# Revit family: Condensing-Solar-Storage-Water-Heater-Gas_AO_Smith-SGS_30_PF
name_source: partatom
category: Mechanical Equipment
revit_build: Autodesk Revit 2014 (Build: 20130308_1515(x64)
units: mm (PartAtom-declared; Revit-internal decimal feet)

## types (1)
- Condensing-Solar-Storage-Water-Heater-Gas_AO_Smith-SGS_30_PF
    (Contrôle supplémentaires) Fréquence secteur (± 1 Hz) = 50 Hz
    (Contrôle supplémentaires) Phase = 1
    (Contrôle supplémentaires) Puissance Électrique Absorbée = 700 W
    (Contrôle supplémentaires) Tension d'Alimentation (-15%, +10%) = 230 V
    1er Entretien (check-up) = 3 mois après l'installation
    2ème Entretien (Entretien Général) = 12 mois après l'installation
    Assembly Code = D3010
    BIM Content Developer = CAD & Company
    CE-PIN = 0063BU3889
    CO2-émissions (tol. ± 1.0) = 10.0
    Capacité = 368.0 L
    Catégorie de Gaz = II2Esi3P
    Charge Maximale au Sol = 582 kg
    Charge Nominale (Valeur Inférieure) = 30000 W
    Charge Nominale (Valeur Supérieure) = 32600 W
    Consommation de Gaz - Masse = 2.3
    Consommation de Gaz - Volume = 0
    Description = Préparateur ECS Solaire en Combinaison avec Réservoir de Stockage
    Destination / Pays = France
    Diamètre = 705 mm
    Diamètre Cheminée - Boiler = 100/150 mm/mm
    Diamètre Cheminée - Système Concentrique = 100/150 mm/mm
    Diamètre Cheminée - Système Parallèle = 100 mm  [stored 0.328084 ft]
    Débit de vidage en Continu à ΔT = 28°C = 1100.0 L/s
    Débit de vidage en Continu à ΔT = 44°C = 640.0 L/s
    Débit de vidage en Continu à ΔT = 50°C = 570.0 L/s
    Débit de vidage en Continu à ΔT = 55°C = 520.0 L/s
    Débit de vidage en Continu à ΔT = 70°C = 0.0 L/s
    Débit de vidage à ΔT = 28°C après 120 min. = 2400.0 L
    Débit de vidage à ΔT = 28°C après 30 min. = 820.0 L
    Débit de vidage à ΔT = 28°C après 60 min. = 1400.0 L
    Débit de vidage à ΔT = 28°C après 90 min. = 1900.0 L
    Débit de vidage à ΔT = 44°C après 120 min. = 1400.0 L
    Débit de vidage à ΔT = 44°C après 30 min. = 440.0 L
    Débit de vidage à ΔT = 44°C après 60 min. = 760.0 L
    Débit de vidage à ΔT = 44°C après 90 min. = 1100.0 L
    Débit de vidage à ΔT = 50°C après 120 min. = 1200.0 L
    Débit de vidage à ΔT = 50°C après 30 min. = 350.0 L
    Débit de vidage à ΔT = 50°C après 60 min. = 640.0 L
    Débit de vidage à ΔT = 50°C après 90 min. = 920.0 L
    Débit de vidage à ΔT = 55°C après 120 min. = 1100.0 L
    Débit de vidage à ΔT = 55°C après 30 min. = 290.0 L
    Débit de vidage à ΔT = 55°C après 60 min. = 550.0 L
    Débit de vidage à ΔT = 55°C après 90 min. = 800.0 L
    Débit de vidage à ΔT = 70°C après 120 min. = 0.0 L
    Débit de vidage à ΔT = 70°C après 30 min. = 0.0 L
    Débit de vidage à ΔT = 70°C après 60 min. = 0.0 L
    Débit de vidage à ΔT = 70°C après 90 min. = 0.0 L
    Epaisseur d'Isolation = 50 mm  [stored 0.164042 ft]
    Fabricant No. = E 7110
    Fréquence secteur (± 1 Hz) = 50 Hz
    Garantie Pièces = 12 mois
    Garantie sur la Cuve = 36 mois
    Guide de Produit = https://www.aosmithinternational.com
    Hauteur = 2005 mm
    Hauteur Conduit d'Alimentation en Air = 2000 mm  [stored 6.56168 ft]
    Hauteur Conduit d'Évacuation des Fumées = 2000 mm  [stored 6.56168 ft]
    Hauteur d'Emballage = 2055 mm
    Hauteur de l'Alimentation en eau Froide = 255 mm  [stored 0.836614 ft]
    Hauteur de la Sortie d'eau Chaude = 2005 mm
    Hauteur du Raccordement au Gaz = 1810 mm  [stored 5.93832 ft]
    Largeur = 850 mm
    Largeur d'Emballage = 870 mm  [stored 2.85433 ft]
    Manufacturer = A.O. Smith Water Products Company b.v.
    Model = SGS 30 PF
    NOX-émissions = 74
    NOX-émissions (ven air, 0% O2) = 41
    Niveau du Son = 45
    Pertes en Veille = 0 W
    Pertes en Veille - tous les jours (24h) = 0 W
    Phase = 1
    Poids de Transport = 259 kg
    Poids à vide = 239 kg
    Pression Amont de Gaz = 3700
    Pression Différentielle d'Ouverture de l'Interrupteur de Pression = 115.0 Pa
    Pression de Fonctionnement Maximale = 800000.0 Pa
    Production Nominale = 32700 W
    Profondeur = 925 mm
    Profondeur d'Emballage = 950 mm
    Puissance Électrique Absorbée = 45 W
    Raccord Robinet de Vidange = 1"
    Raccord d'Alimentation en Eau Froide = 1 1/2"
    Raccord de Gaz = 3/4"
    Raccord de Sortie d'Eau Chaude = 1 1/2"
    Raccord de la Soupape de Vidange = 1"
    Raccord Évacuation de la Condensation = 40 mm  [stored 0.131234 ft]
    Rendement (Hi, acc. NEN-EN 89 - 1999) = 109
    Rendement (Hs, acc. NEN-EN 89 - 1999) = 98
    Rendement Saisonnier (Hs) = 98
    Réglage Standard Pour = G31
    Serial Number = 8717449193317
    Spécifications du Produit = https://www.aosmithinternational.com
    Temps de réchauffement à ΔT = 28°C = 22
    Temps de réchauffement à ΔT = 44°C = 35
    Temps de réchauffement à ΔT = 50°C = 39
    Temps de réchauffement à ΔT = 55°C = 43
    Température Maximale des Fumées = 50 °C
    Tension d'Alimentation (-15%, +10%) = 230 V
    Type d'Emballage = Plastique Emballage Rétractable, Carton et Bois
    Type d'Installation = B23/C13/C33/C43/C53/C63
    URL = http://www.aosmith.fr
    Valeur Défaut du Thermostat de Régulation = 65 °C
    Valeur Manimale du Thermostat de Régulation = 40 °C
    Valeur Maximale du Thermostat de Régulation = 80 °C
    l'Intervalle d'Entretien = 12 mois

note: [stored X ft] marks values corroborated as IEEE doubles in the binary element streams (Revit-internal decimal feet)

## geometry (parser evidence)
native form markers: Blend x24, Sweep x35
no freeform markers — native parametric forms only
